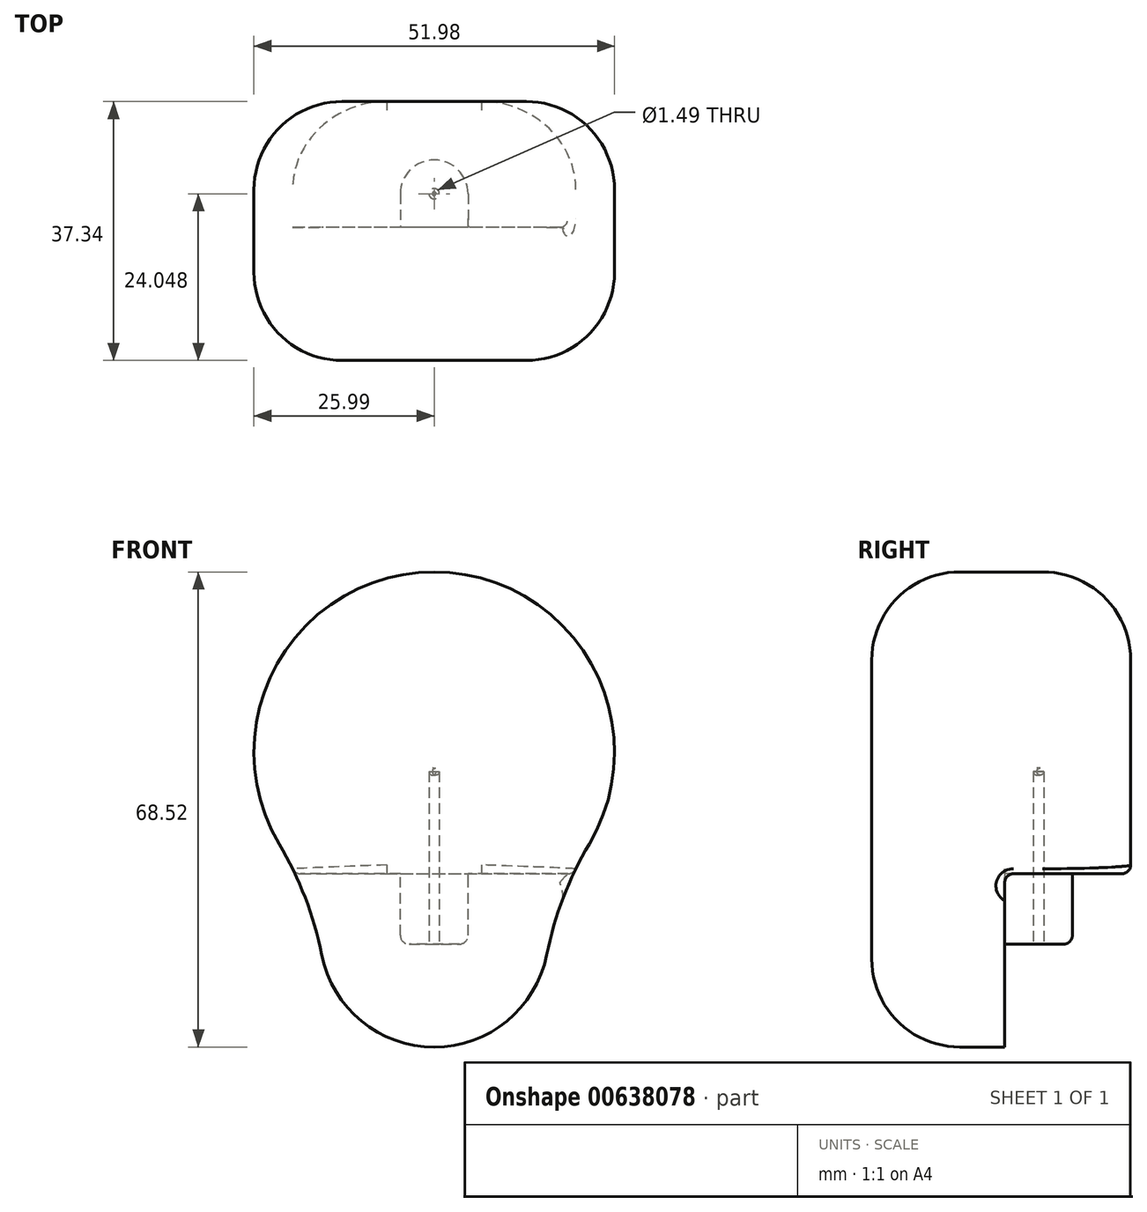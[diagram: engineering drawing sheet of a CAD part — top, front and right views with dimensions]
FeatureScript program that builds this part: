
annotation { "Feature Type Name" : "Feature", "Feature Type Description" : "" }
export const myFeature = defineFeature(function(context is Context, id is Id, definition is map)
    precondition{}
    {
        {
            var Q0;
            Q0=qCreatedBy(makeId("Front.planeOp"),FACE);
            var sketch = newSketch(context, id + "F0", { "sketchPlane" : qUnion([Q0])});
            skCircle(sketch, "E0", {"center": v(0, 0) * mm, "radius": 26 * mm});
            skCircle(sketch, "E1", {"center": v(0, -26) * mm, "radius": 16.54 * mm});
            skSolve(sketch);
        }
        {
            var Q0;
            {var subQ0=sQuery(id+"F0.wireOp",EDGE,"E1");var subQ1=sQuery(id+"F0.wireOp",EDGE,"E0");var subQ2=makeQuery(id+"F0.imprint","INTERSECT",VERTEX,{"disambiguationData":[OD(0.0)],"derivedFrom":[subQ1,subQ0]});Q0=makeQuery(id+"F0.imprint","IMPRINT",FACE,{"disambiguationData":[TD([[makeQuery(id+"F0.imprint","IMPRINT",EDGE,{"disambiguationData":[TD([[subQ2,1.0]])],"derivedFrom":subQ1}),1.0]])]});}
            var Q1;
            {var subQ0=sQuery(id+"F0.wireOp",EDGE,"E1");var subQ1=sQuery(id+"F0.wireOp",EDGE,"E0");var subQ2=makeQuery(id+"F0.imprint","INTERSECT",VERTEX,{"disambiguationData":[OD(0.0)],"derivedFrom":[subQ1,subQ0]});Q1=makeQuery(id+"F0.imprint","IMPRINT",FACE,{"disambiguationData":[TD([[makeQuery(id+"F0.imprint","IMPRINT",EDGE,{"disambiguationData":[TD([[subQ2,-1.0]])],"derivedFrom":subQ1}),1.0]])]});}
            var Q2;
            {var subQ0=sQuery(id+"F0.wireOp",EDGE,"E1");var subQ1=sQuery(id+"F0.wireOp",EDGE,"E0");var subQ2=makeQuery(id+"F0.imprint","INTERSECT",VERTEX,{"disambiguationData":[OD(0.0)],"derivedFrom":[subQ1,subQ0]});Q2=makeQuery(id+"F0.imprint","IMPRINT",FACE,{"disambiguationData":[TD([[makeQuery(id+"F0.imprint","IMPRINT",EDGE,{"disambiguationData":[TD([[subQ2,-1.0]])],"derivedFrom":subQ1}),-1.0]])]});}
            extrude(context, id + "F1", {"entities" : qUnion([Q0, Q1, Q2]), "oppositeDirection" : true, "depth" : 37.34 * mm, "offsetDistance" : 25.4 * mm});
        }
        {
            var Q0;
            {var subQ0=sQuery(id+"F0.wireOp",EDGE,"E1");var subQ1=sQuery(id+"F0.wireOp",EDGE,"E0");Q0=makeQuery(id+"F1.opExtrude","SWEPT_EDGE",EDGE,{"disambiguationData":[OSD([subQ1,subQ0]),TDD([makeQuery(id+"F0.imprint","INTERSECT",VERTEX,{"disambiguationData":[OD(0.0)],"derivedFrom":[subQ1,subQ0]})])]});}
            var Q1;
            {var subQ0=sQuery(id+"F0.wireOp",EDGE,"E1");var subQ1=sQuery(id+"F0.wireOp",EDGE,"E0");Q1=makeQuery(id+"F1.opExtrude","SWEPT_EDGE",EDGE,{"disambiguationData":[OSD([subQ1,subQ0]),TDD([makeQuery(id+"F0.imprint","INTERSECT",VERTEX,{"disambiguationData":[OD(1.0)],"derivedFrom":[subQ1,subQ0]})])]});}
            fillet(context, id + "F2", {"entities" : qUnion([Q0, Q1]), "radius" : 50.8 * mm, "tangentPropagation" : true, "allowEdgeOverflow" : false});
        }
        {
            var Q0;
            Q0=qCreatedBy(makeId("Right.planeOp"),FACE);
            var sketch = newSketch(context, id + "F3", { "sketchPlane" : qUnion([Q0])});
            skLineSegment(sketch, "E2.bottom", {"start": v(49.04, -17.54) * mm, "end": v(19.17, -17.54) * mm});
            skLineSegment(sketch, "E2.top", {"start": v(49.04, -43.9) * mm, "end": v(19.17, -43.9) * mm});
            skLineSegment(sketch, "E2.left", {"start": v(49.04, -17.54) * mm, "end": v(49.04, -43.9) * mm});
            skLineSegment(sketch, "E2.right", {"start": v(19.17, -17.54) * mm, "end": v(19.17, -43.9) * mm});
            skSolve(sketch);
        }
        {
            var Q0;
            Q0=makeQuery(id+"F3.imprint","IMPRINT",FACE,{"disambiguationData":[TD([[makeQuery(id+"F3.imprint","IMPRINT",EDGE,{"derivedFrom":sQuery(id+"F3.wireOp",EDGE,"E2.bottom")}),1.0]])]});
            extrude(context, id + "F4", {"entities" : qUnion([Q0]), "operationType" : NewBodyOperationType.REMOVE, "endBound" : BoundingType.SYMMETRIC, "depth" : 50.8 * mm, "offsetDistance" : 25.4 * mm});
        }
        {
            var Q0;
            Q0=makeQuery(id+"F1.opExtrude","CAP_EDGE",EDGE,{"disambiguationData":[OSD([sQuery(id+"F0.wireOp",EDGE,"E0")])],"isStart":false});
            var Q1;
            Q1=makeQuery(id+"F1.opExtrude","CAP_FACE",FACE,{"disambiguationData":[OSD([sQuery(id+"F0.wireOp",EDGE,"E0"),sQuery(id+"F0.wireOp",EDGE,"E1")])],"isStart":true});
            fillet(context, id + "F5", {"entities" : qUnion([Q0, Q1]), "radius" : 12.7 * mm, "tangentPropagation" : true, "allowEdgeOverflow" : false});
        }
        {
            var Q0;
            Q0=makeQuery(id+"F4.boolean.opBoolean","COPY",FACE,{"derivedFrom":makeQuery(id+"F4.opExtrude","SWEPT_FACE",FACE,{"disambiguationData":[OSD([sQuery(id+"F3.wireOp",EDGE,"E2.bottom")])]})});
            var sketch = newSketch(context, id + "F6", { "sketchPlane" : qUnion([Q0])});
            skLineSegment(sketch, "E3", {"start": v(0, -37.34) * mm, "end": v(0, -19.17) * mm});
            skCircle(sketch, "E4", {"center": v(0, -24.05) * mm, "radius": 4.88 * mm});
            skLineSegment(sketch, "E5", {"start": v(-4.88, -24.05) * mm, "end": v(-4.88, -19.17) * mm});
            skLineSegment(sketch, "E6", {"start": v(4.88, -24.05) * mm, "end": v(4.88, -19.17) * mm});
            skSolve(sketch);
        }
        {
            var Q0;
            {var subQ0=sQuery(id+"F6.wireOp",EDGE,"E4");var subQ1=sQuery(id+"F6.wireOp",EDGE,"E3");var subQ3=makeQuery(id+"F6.imprint","INTERSECT",VERTEX,{"derivedFrom":[subQ1,subQ0]});Q0=makeQuery(id+"F6.imprint","IMPRINT",FACE,{"disambiguationData":[TD([[makeQuery(id+"F6.imprint","IMPRINT",EDGE,{"disambiguationData":[TD([[subQ3,-1.0]])],"derivedFrom":subQ1}),1.0]])]});}
            var Q1;
            {var subQ0=sQuery(id+"F6.wireOp",EDGE,"E4");var subQ1=sQuery(id+"F6.wireOp",EDGE,"E3");var subQ3=makeQuery(id+"F6.imprint","INTERSECT",VERTEX,{"derivedFrom":[subQ1,subQ0]});Q1=makeQuery(id+"F6.imprint","IMPRINT",FACE,{"disambiguationData":[TD([[makeQuery(id+"F6.imprint","IMPRINT",EDGE,{"disambiguationData":[TD([[subQ3,-1.0]])],"derivedFrom":subQ1}),-1.0]])]});}
            var Q2;
            {var subQ3=sQuery(id+"F6.wireOp",EDGE,"E5");Q2=makeQuery(id+"F6.imprint","IMPRINT",FACE,{"disambiguationData":[TD([[makeQuery(id+"F6.imprint","IMPRINT",EDGE,{"derivedFrom":subQ3}),-1.0]])]});}
            var Q3;
            {var subQ3=sQuery(id+"F6.wireOp",EDGE,"E6");Q3=makeQuery(id+"F6.imprint","IMPRINT",FACE,{"disambiguationData":[TD([[makeQuery(id+"F6.imprint","IMPRINT",EDGE,{"derivedFrom":subQ3}),1.0]])]});}
            extrude(context, id + "F7", {"entities" : qUnion([Q0, Q1, Q2, Q3]), "operationType" : NewBodyOperationType.ADD, "depth" : 10.16 * mm, "offsetDistance" : 25.4 * mm});
        }
        {
            var Q0;
            Q0=makeQuery(id+"F7.opExtrude","CAP_FACE",FACE,{"disambiguationData":[OSD([sQuery(id+"F3.wireOp",EDGE,"E2.bottom"),sQuery(id+"F3.wireOp",EDGE,"E2.right"),sQuery(id+"F6.wireOp",EDGE,"E4"),sQuery(id+"F6.wireOp",EDGE,"E5"),sQuery(id+"F6.wireOp",EDGE,"E6")])],"isStart":false});
            var sketch = newSketch(context, id + "F8", { "sketchPlane" : qUnion([Q0])});
            skCircle(sketch, "E7", {"center": v(0, -24.05) * mm, "radius": 0.75 * mm});
            skSolve(sketch);
        }
        {
            var Q0;
            Q0=makeQuery(id+"F8.imprint","IMPRINT",FACE,{"disambiguationData":[TD([[makeQuery(id+"F8.imprint","IMPRINT",EDGE,{"derivedFrom":sQuery(id+"F8.wireOp",EDGE,"E7")}),1.0]])]});
            extrude(context, id + "F9", {"entities" : qUnion([Q0]), "operationType" : NewBodyOperationType.REMOVE, "oppositeDirection" : true, "depth" : 25.4 * mm, "offsetDistance" : 25.4 * mm});
        }
        {
            var Q0;
            Q0=makeQuery(id+"F9.boolean.opBoolean","COPY",EDGE,{"derivedFrom":makeQuery(id+"F9.opExtrude","CAP_EDGE",EDGE,{"disambiguationData":[OSD([sQuery(id+"F8.wireOp",EDGE,"E7")])],"isStart":false})});
            fillet(context, id + "F10", {"entities" : qUnion([Q0]), "radius" : 0.5 * mm, "tangentPropagation" : true, "allowEdgeOverflow" : false});
        }
        {
            var Q0;
            Q0=makeQuery(id+"F9.boolean.opBoolean","COPY",EDGE,{"derivedFrom":makeQuery(id+"F9.opExtrude","CAP_EDGE",EDGE,{"disambiguationData":[OSD([sQuery(id+"F8.wireOp",EDGE,"E7")])],"isStart":true})});
            var Q1;
            Q1=makeQuery(id+"F7.opExtrude","CAP_EDGE",EDGE,{"disambiguationData":[OSD([sQuery(id+"F6.wireOp",EDGE,"E4")])],"isStart":false});
            var Q2;
            Q2=makeQuery(id+"F7.opExtrude","SWEPT_EDGE",EDGE,{"disambiguationData":[OSD([sQuery(id+"F3.wireOp",EDGE,"E2.bottom"),sQuery(id+"F3.wireOp",EDGE,"E2.right"),sQuery(id+"F6.wireOp",EDGE,"E6")])]});
            var Q3;
            {var subQ2=sQuery(id+"F3.wireOp",EDGE,"E2.bottom");var subQ3=sQuery(id+"F3.wireOp",EDGE,"E2.right");Q3=makeQuery(id+"F7.boolean.opBoolean","SPLIT",EDGE,{"disambiguationData":[TD([makeQuery(id+"F7.opExtrude","SWEPT_FACE",FACE,{"disambiguationData":[OSD([sQuery(id+"F6.wireOp",EDGE,"E6")])]})])],"derivedFrom":makeQuery(id+"F4.boolean.opBoolean","COPY",EDGE,{"derivedFrom":makeQuery(id+"F4.opExtrude","SWEPT_EDGE",EDGE,{"disambiguationData":[OSD([subQ2,subQ3])]})})});}
            var Q4;
            Q4=makeQuery(id+"F7.opExtrude","CAP_EDGE",EDGE,{"disambiguationData":[OSD([sQuery(id+"F6.wireOp",EDGE,"E4")])],"isStart":true});
            var Q5;
            Q5=makeQuery(id+"F4.boolean.opBoolean","INTERSECT",EDGE,{"derivedFrom":[makeQuery(id+"F1.opExtrude","CAP_FACE",FACE,{"disambiguationData":[OSD([sQuery(id+"F0.wireOp",EDGE,"E0"),sQuery(id+"F0.wireOp",EDGE,"E1")])],"isStart":false}),makeQuery(id+"F4.opExtrude","SWEPT_FACE",FACE,{"disambiguationData":[OSD([sQuery(id+"F3.wireOp",EDGE,"E2.bottom")])]})]});
            fillet(context, id + "F11", {"entities" : qUnion([Q0, Q1, Q2, Q3, Q4, Q5]), "radius" : 1.27 * mm, "tangentPropagation" : true, "allowEdgeOverflow" : false});
        }
    });
